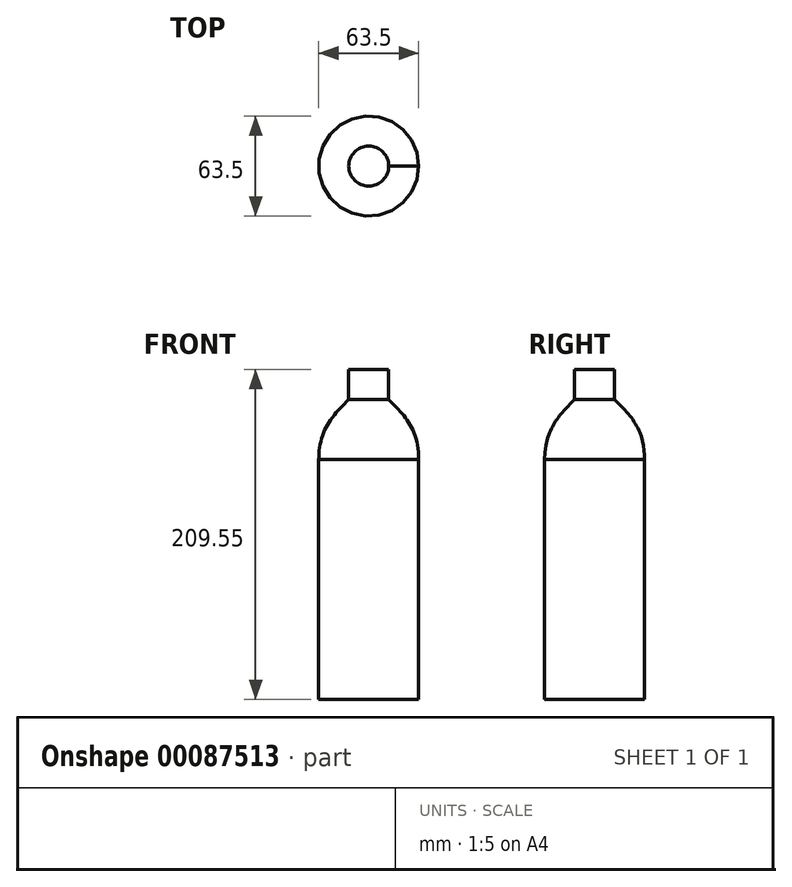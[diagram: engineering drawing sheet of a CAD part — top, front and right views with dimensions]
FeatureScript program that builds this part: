
annotation { "Feature Type Name" : "Feature", "Feature Type Description" : "" }
export const myFeature = defineFeature(function(context is Context, id is Id, definition is map)
    precondition{}
    {
        {
            var Q0;
            Q0=qCreatedBy(makeId("Top.planeOp"),FACE);
            var sketch = newSketch(context, id + "F0", { "sketchPlane" : qUnion([Q0])});
            skCircle(sketch, "E0", {"center": v(0, 0) * mm, "radius": 31.75 * mm});
            skSolve(sketch);
        }
        {
            var Q0;
            Q0 = qSketchRegion(id + "F0", true);
            extrude(context, id + "F1", {"entities" : qUnion([Q0]), "depth" : 152.4 * mm});
        }
        {
            var Q0;
            Q0=makeQuery(id+"F1.opExtrude","CAP_FACE",FACE,{"disambiguationData":[OSD([sQuery(id+"F0.wireOp",EDGE,"E0")])],"isStart":false});
            cPlane(context, id + "F2", {"entities" : qUnion([Q0]), "cplaneType" : CPlaneType.OFFSET, "offset" : 38.1 * mm, "width" : 152.4 * mm, "height" : 152.4 * mm});
        }
        {
            var Q0;
            Q0=qCreatedBy(id+"F2.planeOp",FACE);
            var sketch = newSketch(context, id + "F3", { "sketchPlane" : qUnion([Q0])});
            skCircle(sketch, "E1", {"center": v(0, 0) * mm, "radius": 12.7 * mm});
            skSolve(sketch);
        }
        {
            var Q0;
            Q0=makeQuery(id+"F3.imprint","IMPRINT",FACE,{"disambiguationData":[TD([[makeQuery(id+"F3.imprint","IMPRINT",EDGE,{"derivedFrom":sQuery(id+"F3.wireOp",EDGE,"E1")}),1.0]])]});
            var Q1;
            Q1=makeQuery(id+"F1.opExtrude","CAP_FACE",FACE,{"disambiguationData":[OSD([sQuery(id+"F0.wireOp",EDGE,"E0")])],"isStart":false});
            loft(context, id + "F4", {"operationType" : NewBodyOperationType.ADD, "startCondition" : LoftEndDerivativeType.NORMAL_TO_PROFILE, "startMagnitude" : 0, "endCondition" : LoftEndDerivativeType.NORMAL_TO_PROFILE, "endMagnitude" : 1.5, "sheetProfilesArray" : [{ "sheetProfileEntities" : qUnion([Q0]) }, { "sheetProfileEntities" : qUnion([Q1]) }]});
        }
        {
            var Q0;
            Q0=makeQuery(id+"F4.opLoft","CAP_FACE",FACE,{"disambiguationData":[OSD([makeQuery(id+"F3.imprint","IMPRINT",FACE,{"disambiguationData":[TD([[makeQuery(id+"F3.imprint","IMPRINT",EDGE,{"derivedFrom":sQuery(id+"F3.wireOp",EDGE,"E1")}),1.0]])]})])],"isStart":true});
            extrude(context, id + "F5", {"entities" : qUnion([Q0]), "operationType" : NewBodyOperationType.ADD, "depth" : 19.05 * mm});
        }
    });
